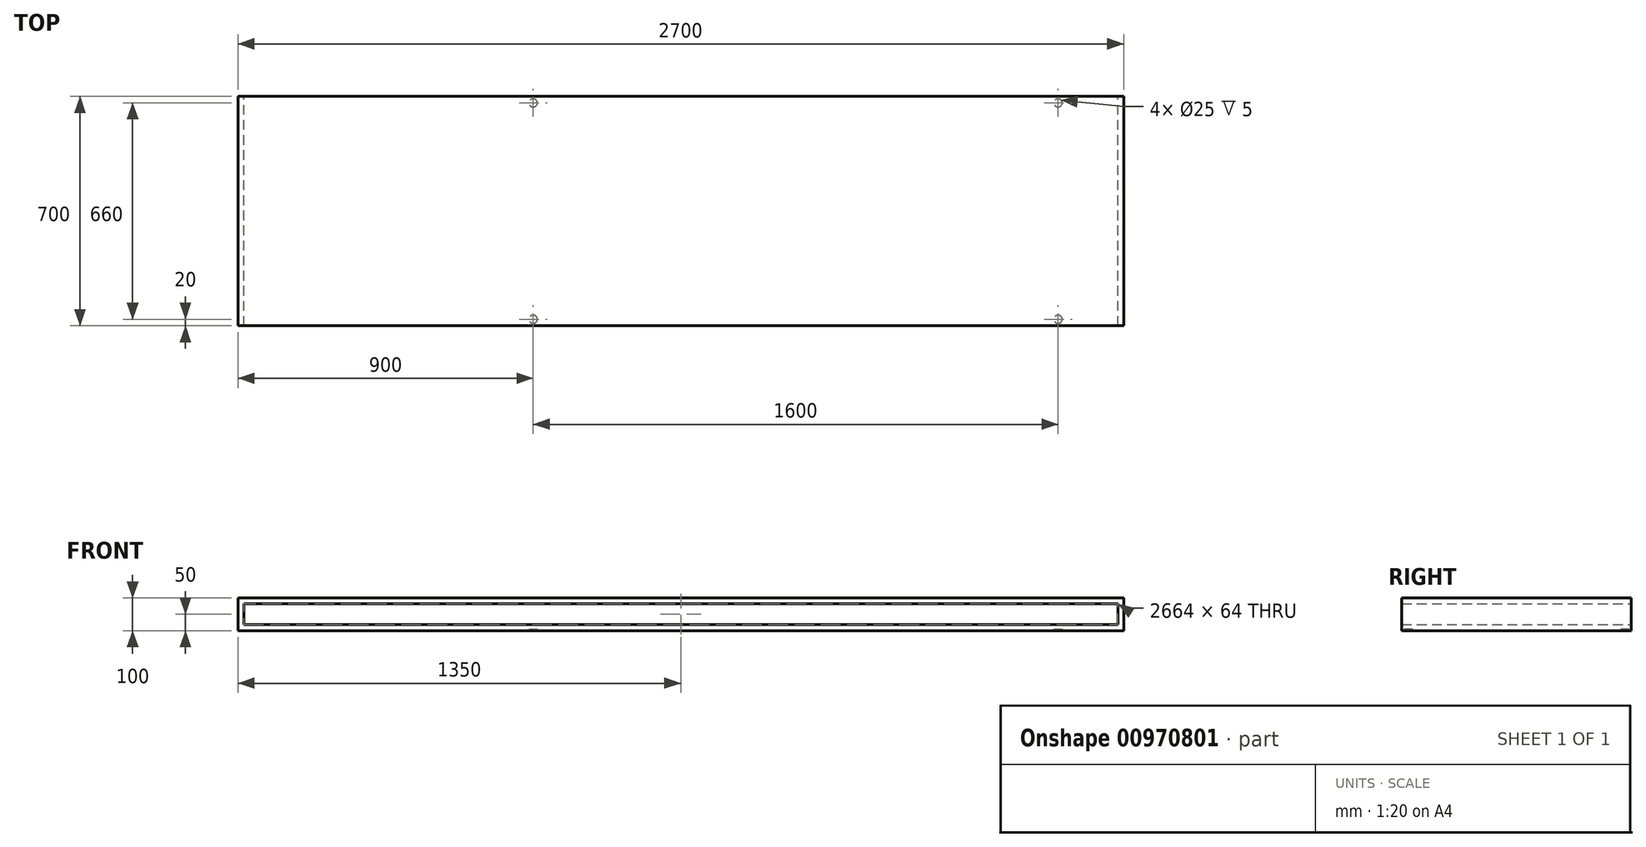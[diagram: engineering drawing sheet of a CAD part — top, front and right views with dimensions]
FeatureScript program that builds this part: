
annotation { "Feature Type Name" : "Feature", "Feature Type Description" : "" }
export const myFeature = defineFeature(function(context is Context, id is Id, definition is map)
    precondition{}
    {
        {
            var Q0;
            Q0=qCreatedBy(makeId("Front.planeOp"),FACE);
            var sketch = newSketch(context, id + "F0", { "sketchPlane" : qUnion([Q0])});
            skLineSegment(sketch, "E0.bottom", {"start": v(-1350, 0) * mm, "end": v(1350, 0) * mm});
            skLineSegment(sketch, "E0.top", {"start": v(-1350, 100) * mm, "end": v(1350, 100) * mm});
            skLineSegment(sketch, "E0.left", {"start": v(-1350, 0) * mm, "end": v(-1350, 100) * mm});
            skLineSegment(sketch, "E0.right", {"start": v(1350, 0) * mm, "end": v(1350, 100) * mm});
            skLineSegment(sketch, "E1.bottom", {"start": v(1332, 82) * mm, "end": v(-1332, 82) * mm});
            skLineSegment(sketch, "E1.top", {"start": v(1332, 18) * mm, "end": v(-1332, 18) * mm});
            skLineSegment(sketch, "E1.left", {"start": v(1332, 82) * mm, "end": v(1332, 18) * mm});
            skLineSegment(sketch, "E1.right", {"start": v(-1332, 82) * mm, "end": v(-1332, 18) * mm});
            skSolve(sketch);
        }
        {
            var Q0;
            Q0=qSketchRegion(id+"F0",true);
            extrude(context, id + "F1", {"entities" : qUnion([Q0]), "endBound" : BoundingType.SYMMETRIC, "depth" : 700 * mm, "offsetDistance" : 25 * mm});
        }
        {
            var Q0;
            Q0=makeQuery(id+"F1.opExtrude","SWEPT_FACE",FACE,{"disambiguationData":[OSD([sQuery(id+"F0.wireOp",EDGE,"E0.bottom")])]});
            var sketch = newSketch(context, id + "F2", { "sketchPlane" : qUnion([Q0])});
            skCircle(sketch, "E2", {"center": v(-450, 330) * mm, "radius": 12.5 * mm});
            skCircle(sketch, "E3", {"center": v(-450, -330) * mm, "radius": 12.5 * mm});
            skCircle(sketch, "E4", {"center": v(1150, 330) * mm, "radius": 12.5 * mm});
            skCircle(sketch, "E5", {"center": v(1150, -330) * mm, "radius": 12.5 * mm});
            skSolve(sketch);
        }
        {
            var Q0;
            Q0 = qSketchRegion(id + "F2", true);
            extrude(context, id + "F3", {"entities" : qUnion([Q0]), "operationType" : NewBodyOperationType.REMOVE, "oppositeDirection" : true, "depth" : 5 * mm, "offsetDistance" : 25 * mm});
        }
    });
